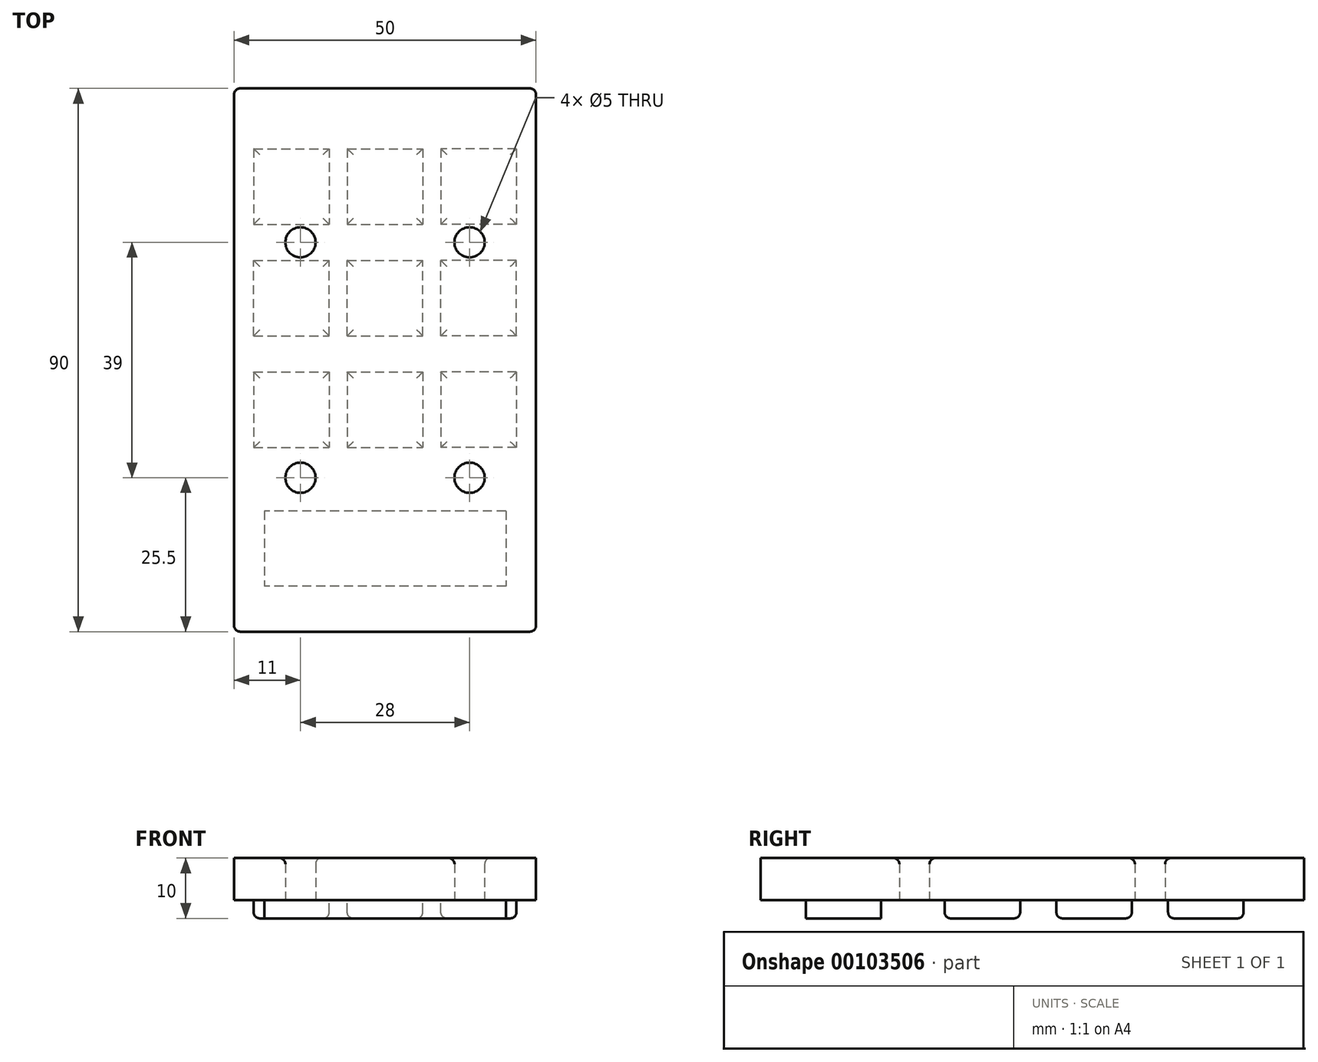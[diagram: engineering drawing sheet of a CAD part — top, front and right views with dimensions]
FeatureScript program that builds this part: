
annotation { "Feature Type Name" : "Feature", "Feature Type Description" : "" }
export const myFeature = defineFeature(function(context is Context, id is Id, definition is map)
    precondition{}
    {
        {
            var Q0;
            Q0=qCreatedBy(makeId("Front.planeOp"),FACE);
            var sketch = newSketch(context, id + "F0", { "sketchPlane" : qUnion([Q0])});
            skLineSegment(sketch, "E0", {"start": v(0, 0) * mm, "end": v(-25, 0) * mm});
            skLineSegment(sketch, "E1", {"start": v(-25, 0) * mm, "end": v(-25, 7) * mm});
            skLineSegment(sketch, "E2", {"start": v(-25, 7) * mm, "end": v(25, 7) * mm});
            skLineSegment(sketch, "E3", {"start": v(25, 7) * mm, "end": v(25, 0) * mm});
            skLineSegment(sketch, "E4", {"start": v(25, 0) * mm, "end": v(0, 0) * mm});
            skSolve(sketch);
        }
        {
            var Q0;
            Q0 = qSketchRegion(id + "F0", true);
            extrude(context, id + "F1", {"entities" : qUnion([Q0]), "endBound" : BoundingType.SYMMETRIC, "depth" : 90 * mm});
        }
        {
            var Q0;
            Q0=qCreatedBy(makeId("Top.planeOp"),FACE);
            var sketch = newSketch(context, id + "F2", { "sketchPlane" : qUnion([Q0])});
            skLineSegment(sketch, "E5.bottom", {"start": v(-6.25, 35) * mm, "end": v(6.25, 35) * mm});
            skLineSegment(sketch, "E5.top", {"start": v(-6.25, 22.5) * mm, "end": v(6.25, 22.5) * mm});
            skLineSegment(sketch, "E5.left", {"start": v(-6.25, 35) * mm, "end": v(-6.25, 22.5) * mm});
            skLineSegment(sketch, "E5.right", {"start": v(6.25, 35) * mm, "end": v(6.25, 22.5) * mm});
            skLineSegment(sketch, "E6.bottom", {"start": v(-21.75, 35) * mm, "end": v(-9.25, 35) * mm});
            skLineSegment(sketch, "E6.top", {"start": v(-21.75, 22.5) * mm, "end": v(-9.25, 22.5) * mm});
            skLineSegment(sketch, "E6.left", {"start": v(-21.75, 35) * mm, "end": v(-21.75, 22.5) * mm});
            skLineSegment(sketch, "E6.right", {"start": v(-9.25, 35) * mm, "end": v(-9.25, 22.5) * mm});
            skLineSegment(sketch, "E7", {"start": v(0, 60.89) * mm, "end": v(0, -50.2) * mm, "construction": true});
            skLineSegment(sketch, "E8.MirrorCS", {"start": v(9.25, 35) * mm, "end": v(9.25, 22.5) * mm});
            skLineSegment(sketch, "E9.MirrorCS", {"start": v(21.75, 35) * mm, "end": v(9.25, 35) * mm});
            skLineSegment(sketch, "E10.MirrorCS", {"start": v(21.75, 22.5) * mm, "end": v(9.25, 22.5) * mm});
            skLineSegment(sketch, "E11.MirrorCS", {"start": v(21.75, 35) * mm, "end": v(21.75, 22.5) * mm});
            skLineSegment(sketch, "E12", {"start": v(37.43, 19.5) * mm, "end": v(-56.3, 19.5) * mm, "construction": true});
            skLineSegment(sketch, "E13.MirrorCS", {"start": v(-21.75, 16.5) * mm, "end": v(-9.25, 16.5) * mm});
            skLineSegment(sketch, "E14.MirrorCS", {"start": v(-9.25, 4) * mm, "end": v(-9.25, 16.5) * mm});
            skLineSegment(sketch, "E15.MirrorCS", {"start": v(-21.75, 4) * mm, "end": v(-9.25, 4) * mm});
            skLineSegment(sketch, "E16.MirrorCS", {"start": v(6.25, 4) * mm, "end": v(6.25, 16.5) * mm});
            skLineSegment(sketch, "E17.MirrorCS", {"start": v(21.75, 4) * mm, "end": v(9.25, 4) * mm});
            skLineSegment(sketch, "E18.MirrorCS", {"start": v(9.25, 4) * mm, "end": v(9.25, 16.5) * mm});
            skLineSegment(sketch, "E19.MirrorCS", {"start": v(-21.75, 4) * mm, "end": v(-21.75, 16.5) * mm});
            skLineSegment(sketch, "E20.MirrorCS", {"start": v(-6.25, 16.5) * mm, "end": v(6.25, 16.5) * mm});
            skLineSegment(sketch, "E21.MirrorCS", {"start": v(-6.25, 4) * mm, "end": v(-6.25, 16.5) * mm});
            skLineSegment(sketch, "E22.MirrorCS", {"start": v(21.75, 16.5) * mm, "end": v(9.25, 16.5) * mm});
            skLineSegment(sketch, "E23.MirrorCS", {"start": v(-6.25, 4) * mm, "end": v(6.25, 4) * mm});
            skLineSegment(sketch, "E24.MirrorCS", {"start": v(21.75, 4) * mm, "end": v(21.75, 16.5) * mm});
            skLineSegment(sketch, "E25", {"start": v(41.43, 1) * mm, "end": v(-47.04, 1) * mm, "construction": true});
            skLineSegment(sketch, "E26.MirrorCS", {"start": v(-21.75, -14.5) * mm, "end": v(-9.25, -14.5) * mm});
            skLineSegment(sketch, "E27.MirrorCS", {"start": v(21.75, -2) * mm, "end": v(21.75, -14.5) * mm});
            skLineSegment(sketch, "E28.MirrorCS", {"start": v(-21.75, -2) * mm, "end": v(-9.25, -2) * mm});
            skLineSegment(sketch, "E29.MirrorCS", {"start": v(-9.25, -2) * mm, "end": v(-9.25, -14.5) * mm});
            skLineSegment(sketch, "E30.MirrorCS", {"start": v(-6.25, -14.5) * mm, "end": v(6.25, -14.5) * mm});
            skLineSegment(sketch, "E31.MirrorCS", {"start": v(-21.75, -2) * mm, "end": v(-21.75, -14.5) * mm});
            skLineSegment(sketch, "E32.MirrorCS", {"start": v(21.75, -2) * mm, "end": v(9.25, -2) * mm});
            skLineSegment(sketch, "E33.MirrorCS", {"start": v(6.25, -2) * mm, "end": v(6.25, -14.5) * mm});
            skLineSegment(sketch, "E34.MirrorCS", {"start": v(-6.25, -2) * mm, "end": v(6.25, -2) * mm});
            skLineSegment(sketch, "E35.MirrorCS", {"start": v(9.25, -2) * mm, "end": v(9.25, -14.5) * mm});
            skLineSegment(sketch, "E36.MirrorCS", {"start": v(-6.25, -2) * mm, "end": v(-6.25, -14.5) * mm});
            skLineSegment(sketch, "E37.MirrorCS", {"start": v(21.75, -14.5) * mm, "end": v(9.25, -14.5) * mm});
            skLineSegment(sketch, "E38.bottom", {"start": v(20, -25) * mm, "end": v(-20, -25) * mm});
            skLineSegment(sketch, "E38.top", {"start": v(20, -37.5) * mm, "end": v(-20, -37.5) * mm});
            skLineSegment(sketch, "E38.left", {"start": v(20, -25) * mm, "end": v(20, -37.5) * mm});
            skLineSegment(sketch, "E38.right", {"start": v(-20, -25) * mm, "end": v(-20, -37.5) * mm});
            skSolve(sketch);
        }
        {
            var Q0;
            Q0 = qSketchRegion(id + "F2", true);
            extrude(context, id + "F3", {"entities" : qUnion([Q0]), "operationType" : NewBodyOperationType.ADD, "oppositeDirection" : true, "depth" : 3 * mm});
        }
        {
            var Q0;
            Q0=makeQuery(id+"F1.opExtrude","CAP_EDGE",EDGE,{"disambiguationData":[OSD([sQuery(id+"F0.wireOp",EDGE,"E3")])],"isStart":true});
            var Q1;
            Q1=makeQuery(id+"F1.opExtrude","CAP_EDGE",EDGE,{"disambiguationData":[OSD([sQuery(id+"F0.wireOp",EDGE,"E3")])],"isStart":false});
            var Q2;
            Q2=makeQuery(id+"F1.opExtrude","CAP_EDGE",EDGE,{"disambiguationData":[OSD([sQuery(id+"F0.wireOp",EDGE,"E1")])],"isStart":true});
            var Q3;
            Q3=makeQuery(id+"F1.opExtrude","CAP_EDGE",EDGE,{"disambiguationData":[OSD([sQuery(id+"F0.wireOp",EDGE,"E1")])],"isStart":false});
            var Q4;
            Q4=makeQuery(id+"F3.opExtrude","CAP_EDGE",EDGE,{"disambiguationData":[OSD([sQuery(id+"F2.wireOp",EDGE,"E9.MirrorCS")])],"isStart":false});
            var Q5;
            Q5=makeQuery(id+"F3.opExtrude","CAP_EDGE",EDGE,{"disambiguationData":[OSD([sQuery(id+"F2.wireOp",EDGE,"E11.MirrorCS")])],"isStart":false});
            var Q6;
            Q6=makeQuery(id+"F3.opExtrude","CAP_EDGE",EDGE,{"disambiguationData":[OSD([sQuery(id+"F2.wireOp",EDGE,"E10.MirrorCS")])],"isStart":false});
            var Q7;
            Q7=makeQuery(id+"F3.opExtrude","CAP_EDGE",EDGE,{"disambiguationData":[OSD([sQuery(id+"F2.wireOp",EDGE,"E8.MirrorCS")])],"isStart":false});
            var Q8;
            Q8=makeQuery(id+"F3.opExtrude","CAP_EDGE",EDGE,{"disambiguationData":[OSD([sQuery(id+"F2.wireOp",EDGE,"E5.bottom")])],"isStart":false});
            var Q9;
            Q9=makeQuery(id+"F3.opExtrude","CAP_EDGE",EDGE,{"disambiguationData":[OSD([sQuery(id+"F2.wireOp",EDGE,"E5.right")])],"isStart":false});
            var Q10;
            Q10=makeQuery(id+"F3.opExtrude","CAP_EDGE",EDGE,{"disambiguationData":[OSD([sQuery(id+"F2.wireOp",EDGE,"E5.top")])],"isStart":false});
            var Q11;
            Q11=makeQuery(id+"F3.opExtrude","CAP_EDGE",EDGE,{"disambiguationData":[OSD([sQuery(id+"F2.wireOp",EDGE,"E5.left")])],"isStart":false});
            var Q12;
            Q12=makeQuery(id+"F3.opExtrude","CAP_EDGE",EDGE,{"disambiguationData":[OSD([sQuery(id+"F2.wireOp",EDGE,"E6.right")])],"isStart":false});
            var Q13;
            Q13=makeQuery(id+"F3.opExtrude","CAP_EDGE",EDGE,{"disambiguationData":[OSD([sQuery(id+"F2.wireOp",EDGE,"E6.bottom")])],"isStart":false});
            var Q14;
            Q14=makeQuery(id+"F3.opExtrude","CAP_EDGE",EDGE,{"disambiguationData":[OSD([sQuery(id+"F2.wireOp",EDGE,"E6.top")])],"isStart":false});
            var Q15;
            Q15=makeQuery(id+"F3.opExtrude","CAP_EDGE",EDGE,{"disambiguationData":[OSD([sQuery(id+"F2.wireOp",EDGE,"E6.left")])],"isStart":false});
            var Q16;
            Q16=makeQuery(id+"F3.opExtrude","CAP_EDGE",EDGE,{"disambiguationData":[OSD([sQuery(id+"F2.wireOp",EDGE,"E19.MirrorCS")])],"isStart":false});
            var Q17;
            Q17=makeQuery(id+"F3.opExtrude","CAP_EDGE",EDGE,{"disambiguationData":[OSD([sQuery(id+"F2.wireOp",EDGE,"E13.MirrorCS")])],"isStart":false});
            var Q18;
            Q18=makeQuery(id+"F3.opExtrude","CAP_EDGE",EDGE,{"disambiguationData":[OSD([sQuery(id+"F2.wireOp",EDGE,"E14.MirrorCS")])],"isStart":false});
            var Q19;
            Q19=makeQuery(id+"F3.opExtrude","CAP_EDGE",EDGE,{"disambiguationData":[OSD([sQuery(id+"F2.wireOp",EDGE,"E15.MirrorCS")])],"isStart":false});
            var Q20;
            Q20=makeQuery(id+"F3.opExtrude","CAP_EDGE",EDGE,{"disambiguationData":[OSD([sQuery(id+"F2.wireOp",EDGE,"E21.MirrorCS")])],"isStart":false});
            var Q21;
            Q21=makeQuery(id+"F3.opExtrude","CAP_EDGE",EDGE,{"disambiguationData":[OSD([sQuery(id+"F2.wireOp",EDGE,"E20.MirrorCS")])],"isStart":false});
            var Q22;
            Q22=makeQuery(id+"F3.opExtrude","CAP_EDGE",EDGE,{"disambiguationData":[OSD([sQuery(id+"F2.wireOp",EDGE,"E16.MirrorCS")])],"isStart":false});
            var Q23;
            Q23=makeQuery(id+"F3.opExtrude","CAP_EDGE",EDGE,{"disambiguationData":[OSD([sQuery(id+"F2.wireOp",EDGE,"E23.MirrorCS")])],"isStart":false});
            var Q24;
            Q24=makeQuery(id+"F3.opExtrude","CAP_EDGE",EDGE,{"disambiguationData":[OSD([sQuery(id+"F2.wireOp",EDGE,"E18.MirrorCS")])],"isStart":false});
            var Q25;
            Q25=makeQuery(id+"F3.opExtrude","CAP_EDGE",EDGE,{"disambiguationData":[OSD([sQuery(id+"F2.wireOp",EDGE,"E22.MirrorCS")])],"isStart":false});
            var Q26;
            Q26=makeQuery(id+"F3.opExtrude","CAP_EDGE",EDGE,{"disambiguationData":[OSD([sQuery(id+"F2.wireOp",EDGE,"E24.MirrorCS")])],"isStart":false});
            var Q27;
            Q27=makeQuery(id+"F3.opExtrude","CAP_EDGE",EDGE,{"disambiguationData":[OSD([sQuery(id+"F2.wireOp",EDGE,"E17.MirrorCS")])],"isStart":false});
            var Q28;
            Q28=makeQuery(id+"F3.opExtrude","CAP_EDGE",EDGE,{"disambiguationData":[OSD([sQuery(id+"F2.wireOp",EDGE,"E32.MirrorCS")])],"isStart":false});
            var Q29;
            Q29=makeQuery(id+"F3.opExtrude","CAP_EDGE",EDGE,{"disambiguationData":[OSD([sQuery(id+"F2.wireOp",EDGE,"E27.MirrorCS")])],"isStart":false});
            var Q30;
            Q30=makeQuery(id+"F3.opExtrude","CAP_EDGE",EDGE,{"disambiguationData":[OSD([sQuery(id+"F2.wireOp",EDGE,"E37.MirrorCS")])],"isStart":false});
            var Q31;
            Q31=makeQuery(id+"F3.opExtrude","CAP_EDGE",EDGE,{"disambiguationData":[OSD([sQuery(id+"F2.wireOp",EDGE,"E35.MirrorCS")])],"isStart":false});
            var Q32;
            Q32=makeQuery(id+"F3.opExtrude","CAP_EDGE",EDGE,{"disambiguationData":[OSD([sQuery(id+"F2.wireOp",EDGE,"E33.MirrorCS")])],"isStart":false});
            var Q33;
            Q33=makeQuery(id+"F3.opExtrude","CAP_EDGE",EDGE,{"disambiguationData":[OSD([sQuery(id+"F2.wireOp",EDGE,"E34.MirrorCS")])],"isStart":false});
            var Q34;
            Q34=makeQuery(id+"F3.opExtrude","CAP_EDGE",EDGE,{"disambiguationData":[OSD([sQuery(id+"F2.wireOp",EDGE,"E36.MirrorCS")])],"isStart":false});
            var Q35;
            Q35=makeQuery(id+"F3.opExtrude","CAP_EDGE",EDGE,{"disambiguationData":[OSD([sQuery(id+"F2.wireOp",EDGE,"E30.MirrorCS")])],"isStart":false});
            var Q36;
            Q36=makeQuery(id+"F3.opExtrude","CAP_EDGE",EDGE,{"disambiguationData":[OSD([sQuery(id+"F2.wireOp",EDGE,"E28.MirrorCS")])],"isStart":false});
            var Q37;
            Q37=makeQuery(id+"F3.opExtrude","CAP_EDGE",EDGE,{"disambiguationData":[OSD([sQuery(id+"F2.wireOp",EDGE,"E29.MirrorCS")])],"isStart":false});
            var Q38;
            Q38=makeQuery(id+"F3.opExtrude","CAP_EDGE",EDGE,{"disambiguationData":[OSD([sQuery(id+"F2.wireOp",EDGE,"E26.MirrorCS")])],"isStart":false});
            var Q39;
            Q39=makeQuery(id+"F3.opExtrude","CAP_EDGE",EDGE,{"disambiguationData":[OSD([sQuery(id+"F2.wireOp",EDGE,"E31.MirrorCS")])],"isStart":false});
            fillet(context, id + "F4", {"entities" : qUnion([Q0, Q1, Q2, Q3, Q4, Q5, Q6, Q7, Q8, Q9, Q10, Q11, Q12, Q13, Q14, Q15, Q16, Q17, Q18, Q19, Q20, Q21, Q22, Q23, Q24, Q25, Q26, Q27, Q28, Q29, Q30, Q31, Q32, Q33, Q34, Q35, Q36, Q37, Q38, Q39]), "radius" : 1 * mm, "tangentPropagation" : true, "allowEdgeOverflow" : false});
        }
        {
            var Q0;
            Q0=qCreatedBy(makeId("Top.planeOp"),FACE);
            var sketch = newSketch(context, id + "F5", { "sketchPlane" : qUnion([Q0])});
            skCircle(sketch, "E39", {"center": v(14, 19.5) * mm, "radius": 2.5 * mm});
            skCircle(sketch, "E40", {"center": v(14, -19.5) * mm, "radius": 2.5 * mm});
            skLineSegment(sketch, "E41", {"start": v(0, 52.6) * mm, "end": v(0, -59.29) * mm, "construction": true});
            skCircle(sketch, "E42.MirrorC", {"center": v(-14, -19.5) * mm, "radius": 2.5 * mm});
            skCircle(sketch, "E43.MirrorC", {"center": v(-14, 19.5) * mm, "radius": 2.5 * mm});
            skSolve(sketch);
        }
        {
            var Q0;
            Q0 = qSketchRegion(id + "F5", true);
            extrude(context, id + "F6", {"entities" : qUnion([Q0]), "operationType" : NewBodyOperationType.REMOVE, "depth" : 25 * mm});
        }
        {
            var Q0;
            Q0=makeQuery(id+"F6.boolean.opBoolean","COPY",EDGE,{"derivedFrom":makeQuery(id+"F6.opExtrude","CAP_EDGE",EDGE,{"disambiguationData":[OSD([sQuery(id+"F5.wireOp",EDGE,"E39")])],"isStart":true})});
            var Q1;
            Q1=makeQuery(id+"F6.boolean.opBoolean","COPY",EDGE,{"derivedFrom":makeQuery(id+"F6.opExtrude","CAP_EDGE",EDGE,{"disambiguationData":[OSD([sQuery(id+"F5.wireOp",EDGE,"E43.MirrorC")])],"isStart":true})});
            var Q2;
            Q2=makeQuery(id+"F6.boolean.opBoolean","COPY",EDGE,{"derivedFrom":makeQuery(id+"F6.opExtrude","CAP_EDGE",EDGE,{"disambiguationData":[OSD([sQuery(id+"F5.wireOp",EDGE,"E40")])],"isStart":true})});
            var Q3;
            Q3=makeQuery(id+"F6.boolean.opBoolean","COPY",EDGE,{"derivedFrom":makeQuery(id+"F6.opExtrude","CAP_EDGE",EDGE,{"disambiguationData":[OSD([sQuery(id+"F5.wireOp",EDGE,"E42.MirrorC")])],"isStart":true})});
            var Q4;
            Q4=makeQuery(id+"F6.boolean.opBoolean","INTERSECT",EDGE,{"derivedFrom":[makeQuery(id+"F1.opExtrude","SWEPT_FACE",FACE,{"disambiguationData":[OSD([sQuery(id+"F0.wireOp",EDGE,"E2")])]}),makeQuery(id+"F6.opExtrude","SWEPT_FACE",FACE,{"disambiguationData":[OSD([sQuery(id+"F5.wireOp",EDGE,"E42.MirrorC")])]})]});
            var Q5;
            Q5=makeQuery(id+"F6.boolean.opBoolean","INTERSECT",EDGE,{"derivedFrom":[makeQuery(id+"F1.opExtrude","SWEPT_FACE",FACE,{"disambiguationData":[OSD([sQuery(id+"F0.wireOp",EDGE,"E2")])]}),makeQuery(id+"F6.opExtrude","SWEPT_FACE",FACE,{"disambiguationData":[OSD([sQuery(id+"F5.wireOp",EDGE,"E40")])]})]});
            var Q6;
            Q6=makeQuery(id+"F6.boolean.opBoolean","INTERSECT",EDGE,{"derivedFrom":[makeQuery(id+"F1.opExtrude","SWEPT_FACE",FACE,{"disambiguationData":[OSD([sQuery(id+"F0.wireOp",EDGE,"E2")])]}),makeQuery(id+"F6.opExtrude","SWEPT_FACE",FACE,{"disambiguationData":[OSD([sQuery(id+"F5.wireOp",EDGE,"E39")])]})]});
            var Q7;
            Q7=makeQuery(id+"F6.boolean.opBoolean","INTERSECT",EDGE,{"derivedFrom":[makeQuery(id+"F1.opExtrude","SWEPT_FACE",FACE,{"disambiguationData":[OSD([sQuery(id+"F0.wireOp",EDGE,"E2")])]}),makeQuery(id+"F6.opExtrude","SWEPT_FACE",FACE,{"disambiguationData":[OSD([sQuery(id+"F5.wireOp",EDGE,"E43.MirrorC")])]})]});
            fillet(context, id + "F7", {"entities" : qUnion([Q0, Q1, Q2, Q3, Q4, Q5, Q6, Q7]), "radius" : 1 * mm, "tangentPropagation" : true, "allowEdgeOverflow" : false});
        }
    });
